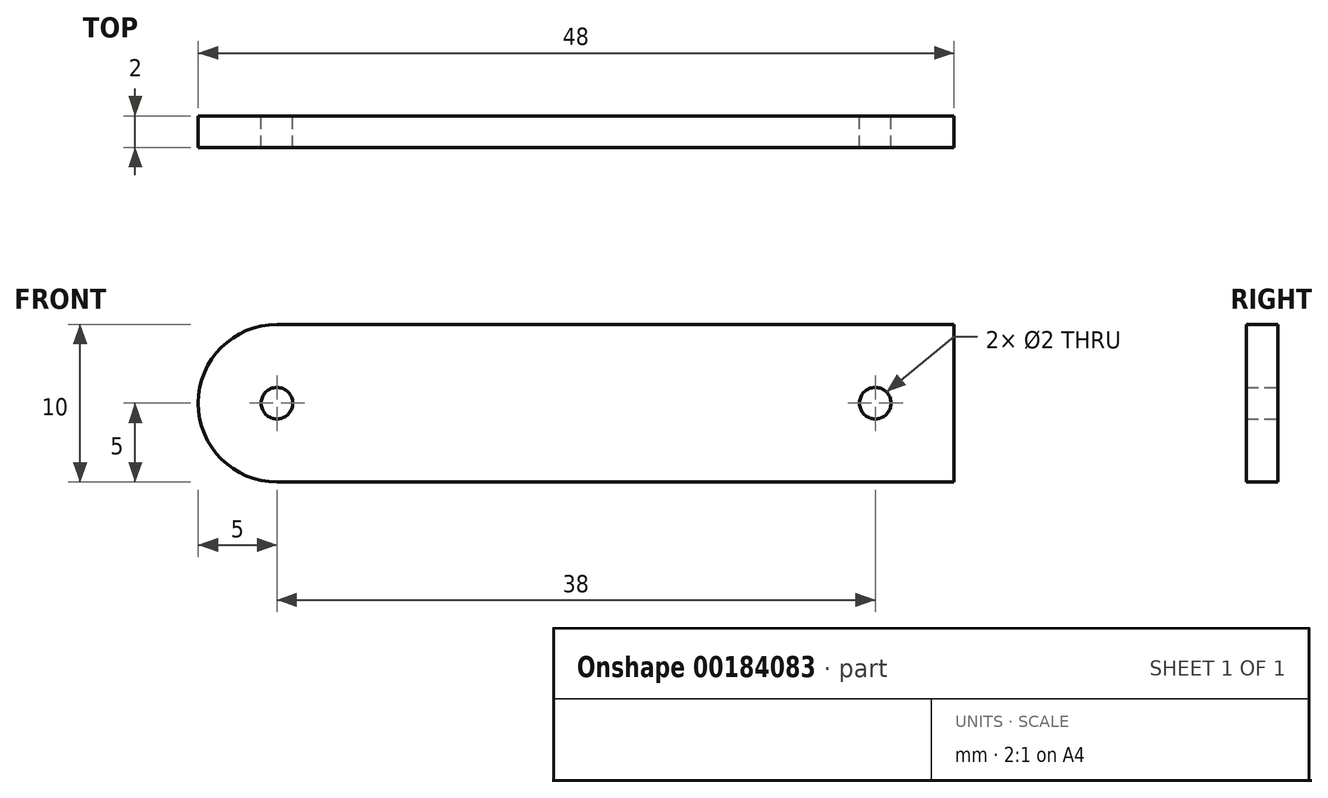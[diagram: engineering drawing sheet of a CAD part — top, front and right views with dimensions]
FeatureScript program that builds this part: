
annotation { "Feature Type Name" : "Feature", "Feature Type Description" : "" }
export const myFeature = defineFeature(function(context is Context, id is Id, definition is map)
    precondition{}
    {
        {
            var Q0;
            Q0=qCreatedBy(makeId("Front.planeOp"),FACE);
            var sketch = newSketch(context, id + "F0", { "sketchPlane" : qUnion([Q0])});
            skLineSegment(sketch, "E0.bottom", {"start": v(0, 0) * mm, "end": v(43, 0) * mm});
            skLineSegment(sketch, "E0.top", {"start": v(0, -10) * mm, "end": v(43, -10) * mm});
            skLineSegment(sketch, "E0.right", {"start": v(43, 0) * mm, "end": v(43, -10) * mm});
            skArc(sketch, "E1", {"start": v(0, 0) * mm, "mid": v(-5, -5) * mm, "end": v(0, -10) * mm});
            skCircle(sketch, "E2", {"center": v(0, -5) * mm, "radius": 1 * mm});
            skCircle(sketch, "E3", {"center": v(38, -5) * mm, "radius": 1 * mm});
            skSolve(sketch);
        }
        {
            var Q0;
            Q0 = qSketchRegion(id + "F0", true);
            extrude(context, id + "F1", {"entities" : qUnion([Q0]), "depth" : 2 * mm});
        }
    });
